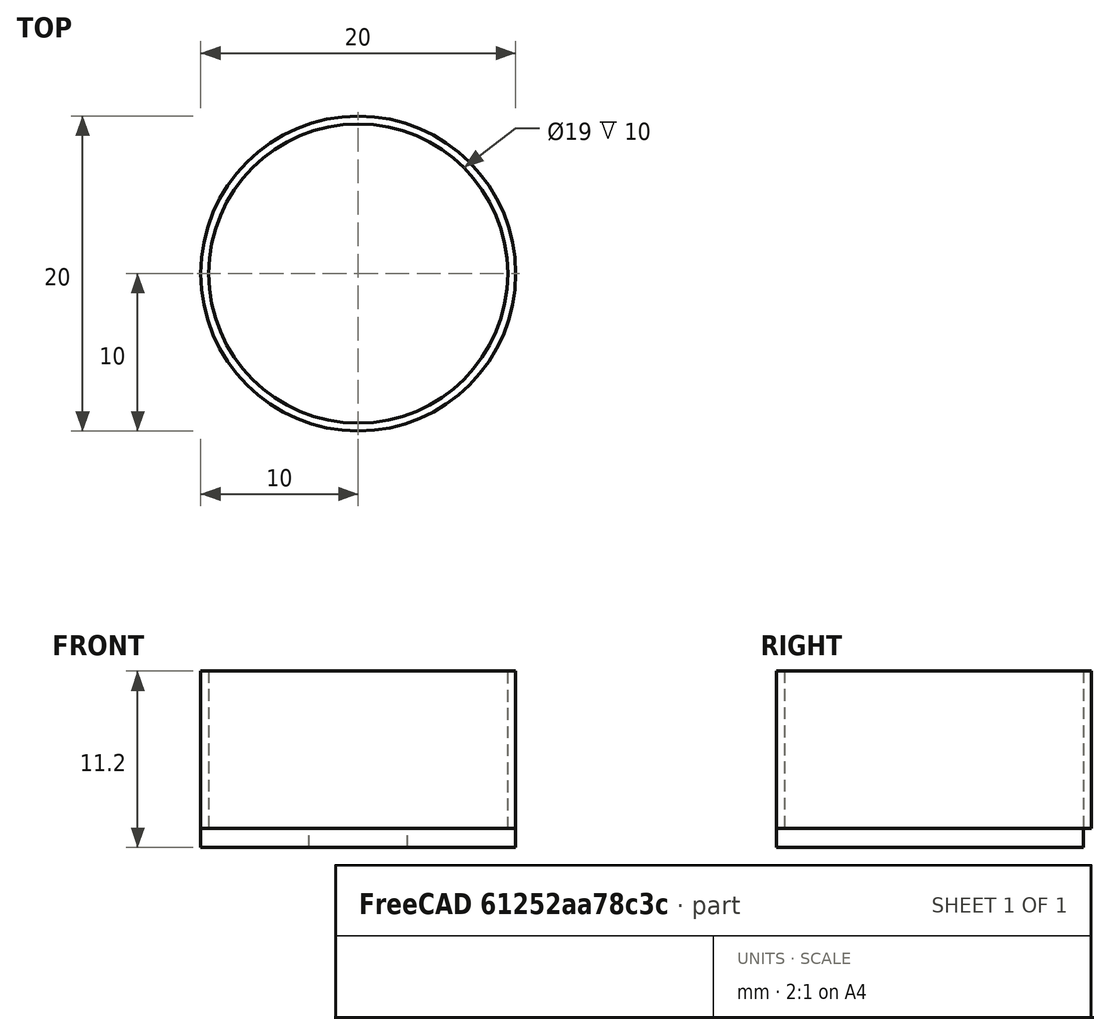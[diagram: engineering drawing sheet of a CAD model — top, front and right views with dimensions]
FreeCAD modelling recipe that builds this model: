
FCSTD DOCUMENT  (FreeCAD 0.16R6712 (Git))
Label: LED_01
License: CreativeCommons Attribution-NonCommercial
LicenseURL: http://creativecommons.org/licenses/by-nc/4.0/
objects: Sketcher::SketchObject×3, Part::Extrusion×2, Part::Circle×1
note: 6 computed .brp shape members not serialized (recipe doc carries the construction recipe); baked Part::Feature solids carry a one-line shape summary decoded from their .brp

FEATURE [Part::Circle] Circle
  Angle0 = 0
  Angle1 = 360
  Radius = 10
FEATURE [Sketcher::SketchObject] Sketch
  sketch-geometry (2):
    g0: ArcOfCircle CenterX=0 CenterY=0 CenterZ=0 NormalX=0 NormalY=0 NormalZ=1 Radius=10 StartAngle=1.88836 EndAngle=7.53642
    g1: LineSegment StartX=-3.1225 StartY=9.5 StartZ=0 EndX=3.1225 EndY=9.5 EndZ=0
  constraints (3):
    c: Horizontal(g1)
    c: Coincident(g1,g0)
    c: Coincident(g1,g0)
FEATURE [Part::Extrusion] Extrude_Sketch  label="Sketch_Extrude"
  Base = -> Sketch
  Dir = (0,0,1.2)
  Solid = true
FEATURE [Sketcher::SketchObject] Sketch001
  Placement = pos=(0,0,1.2) rot=(0,0,1;0rad)
  sketch-geometry (2):
    g0: Circle CenterX=0 CenterY=0 CenterZ=0 NormalX=0 NormalY=0 NormalZ=1 Radius=10
    g1: Circle CenterX=0 CenterY=0 CenterZ=0 NormalX=0 NormalY=0 NormalZ=1 Radius=9.5
  constraints (2):
    c: Coincident(g0,g-1)
    c: Coincident(g1,g-1)
FEATURE [Part::Extrusion] Extrude_Sketch001  label="Sketch001_Extrude"
  Base = -> Sketch001
  Dir = (0,0,10)
  Solid = true
FEATURE [Sketcher::SketchObject] Sketch002
  Placement = pos=(0,0,0) rot=(-1,0,0;4.71239rad)
  sketch-geometry (4):
    g0: ArcOfCircle CenterX=9.99966 CenterY=11.1992 CenterZ=0 NormalX=0 NormalY=0 NormalZ=1 Radius=19.9998 StartAngle=2.0943 EndAngle=3.14155
    g1: LineSegment StartX=-10.0002 StartY=11.2 StartZ=0 EndX=-9.5 EndY=11.2 EndZ=0
    g2: ArcOfCircle CenterX=9.5 CenterY=11.2 CenterZ=0 NormalX=0 NormalY=0 NormalZ=1 Radius=19 StartAngle=2.0944 EndAngle=3.14159
    g3: LineSegment StartX=0 StartY=28.5197 StartZ=0 EndX=0 EndY=27.6545 EndZ=0
  constraints (6):
    c: Coincident(g1,g0)
    c: Horizontal(g1)
    c: Vertical(g3)
    c: PointOnObject(g3,g0)
    c: PointOnObject(g2,g1)
    c: Coincident(g3,g2)
